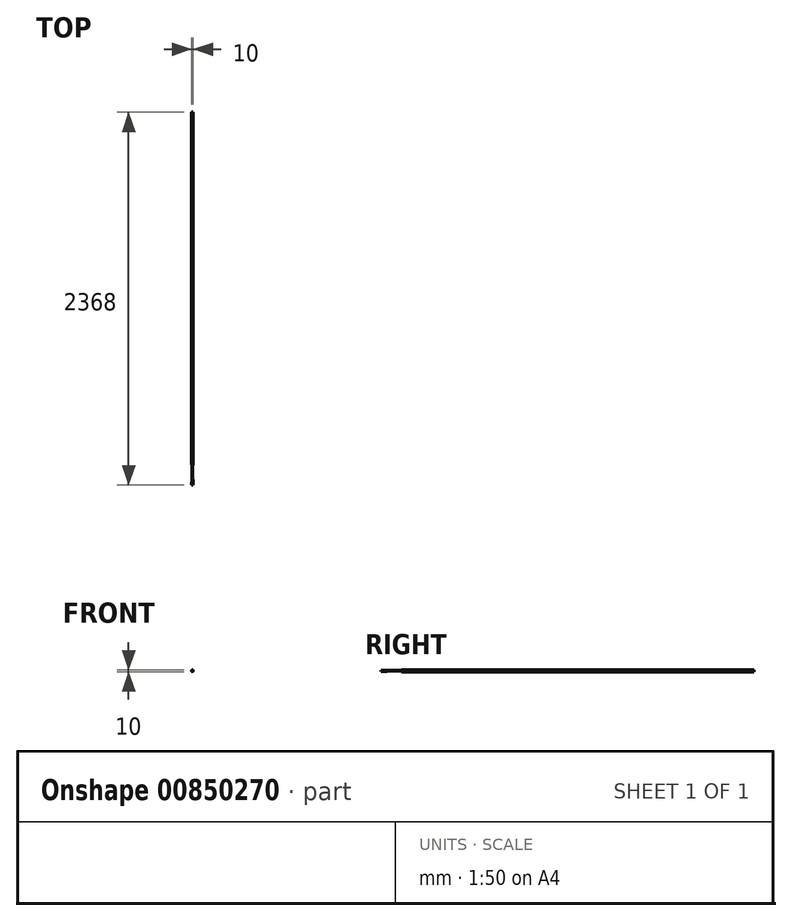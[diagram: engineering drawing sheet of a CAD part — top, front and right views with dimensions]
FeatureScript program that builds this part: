
annotation { "Feature Type Name" : "Feature", "Feature Type Description" : "" }
export const myFeature = defineFeature(function(context is Context, id is Id, definition is map)
    precondition{}
    {
        {
            var Q0;
            Q0=qCreatedBy(makeId("Front.planeOp"),FACE);
            var sketch = newSketch(context, id + "F0", { "sketchPlane" : qUnion([Q0])});
            skLineSegment(sketch, "E0.bottom", {"start": v(5, 3.5) * mm, "end": v(-5, 3.5) * mm});
            skLineSegment(sketch, "E0.top", {"start": v(5, -3.5) * mm, "end": v(-5, -3.5) * mm});
            skLineSegment(sketch, "E0.left", {"start": v(5, 3.5) * mm, "end": v(5, -3.5) * mm});
            skLineSegment(sketch, "E0.right", {"start": v(-5, 3.5) * mm, "end": v(-5, -3.5) * mm});
            skPoint(sketch, "E0.middle", {"position": v(0, 0) * mm});
            skSolve(sketch);
        }
        {
            var Q0;
            Q0 = qSketchRegion(id + "F0", true);
            extrude(context, id + "F1", {"entities" : qUnion([Q0]), "depth" : 20 * mm, "offsetDistance" : 25 * mm});
        }
        {
            var Q0;
            Q0=makeQuery(id+"F1.opExtrude","SWEPT_FACE",FACE,{"disambiguationData":[OSD([sQuery(id+"F0.wireOp",EDGE,"E0.bottom")])]});
            var sketch = newSketch(context, id + "F2", { "sketchPlane" : qUnion([Q0])});
            skLineSegment(sketch, "E1", {"start": v(-7.34, -10) * mm, "end": v(9.17, -10) * mm, "construction": true});
            skLineSegment(sketch, "E2.bottom", {"start": v(2.5, -2) * mm, "end": v(-2.5, -2) * mm});
            skLineSegment(sketch, "E2.top", {"start": v(2.5, -18) * mm, "end": v(-2.5, -18) * mm});
            skLineSegment(sketch, "E2.left", {"start": v(2.5, -2) * mm, "end": v(2.5, -18) * mm});
            skLineSegment(sketch, "E2.right", {"start": v(-2.5, -2) * mm, "end": v(-2.5, -18) * mm});
            skPoint(sketch, "E2.middle", {"position": v(0, -10) * mm});
            skPoint(sketch, "E2.middle.positionSnap0", {"position": v(0.91, -10) * mm});
            skPoint(sketch, "E2.centerSnap0", {"position": v(0.91, -10) * mm});
            skSolve(sketch);
        }
        {
            var Q0;
            Q0 = qSketchRegion(id + "F2", true);
            var Q1;
            Q1=makeQuery(id+"F1.opExtrude","SWEPT_FACE",FACE,{"disambiguationData":[OSD([sQuery(id+"F0.wireOp",EDGE,"E0.top")])]});
            extrude(context, id + "F3", {"entities" : qUnion([Q0]), "operationType" : NewBodyOperationType.REMOVE, "endBound" : BoundingType.UP_TO_SURFACE, "oppositeDirection" : true, "depth" : 10 * mm, "endBoundEntityFace" : qUnion([Q1]), "offsetDistance" : 25 * mm});
        }
        {
            var Q0;
            Q0=makeQuery(id+"F1.opExtrude","SWEPT_FACE",FACE,{"disambiguationData":[OSD([sQuery(id+"F0.wireOp",EDGE,"E0.top")])]});
            var sketch = newSketch(context, id + "F4", { "sketchPlane" : qUnion([Q0])});
            skLineSegment(sketch, "E3.bottom", {"start": v(2.5, 2) * mm, "end": v(-2.5, 2) * mm});
            skLineSegment(sketch, "E3.top", {"start": v(2.5, 5) * mm, "end": v(-2.5, 5) * mm});
            skLineSegment(sketch, "E3.left", {"start": v(2.5, 2) * mm, "end": v(2.5, 5) * mm});
            skLineSegment(sketch, "E3.right", {"start": v(-2.5, 2) * mm, "end": v(-2.5, 5) * mm});
            skLineSegment(sketch, "E4.bottom", {"start": v(-2.5, 18) * mm, "end": v(2.5, 18) * mm});
            skLineSegment(sketch, "E4.top", {"start": v(-2.5, 15) * mm, "end": v(2.5, 15) * mm});
            skLineSegment(sketch, "E4.left", {"start": v(-2.5, 18) * mm, "end": v(-2.5, 15) * mm});
            skLineSegment(sketch, "E4.right", {"start": v(2.5, 18) * mm, "end": v(2.5, 15) * mm});
            skSolve(sketch);
        }
        {
            var Q0;
            Q0 = qSketchRegion(id + "F4", true);
            var Q1;
            Q1=makeQuery(id+"F1.opExtrude","SWEPT_FACE",FACE,{"disambiguationData":[OSD([sQuery(id+"F0.wireOp",EDGE,"E0.bottom")])]});
            extrude(context, id + "F5", {"entities" : qUnion([Q0]), "operationType" : NewBodyOperationType.ADD, "endBound" : BoundingType.UP_TO_SURFACE, "oppositeDirection" : true, "depth" : 25 * mm, "endBoundEntityFace" : qUnion([Q1]), "offsetDistance" : 25 * mm});
        }
        {
            var Q0;
            Q0=makeQuery(id+"F3.boolean.opBoolean","COPY",FACE,{"derivedFrom":makeQuery(id+"F3.opExtrude","SWEPT_FACE",FACE,{"disambiguationData":[OSD([sQuery(id+"F2.wireOp",EDGE,"E2.left")])]})});
            var sketch = newSketch(context, id + "F6", { "sketchPlane" : qUnion([Q0])});
            skLineSegment(sketch, "E5", {"start": v(5, 1.84) * mm, "end": v(2.5, 3.5) * mm});
            skLineSegment(sketch, "E6", {"start": v(2.5, 3.5) * mm, "end": v(5, 3.5) * mm});
            skLineSegment(sketch, "E7", {"start": v(5, 3.5) * mm, "end": v(5, 1.84) * mm});
            skLineSegment(sketch, "E8", {"start": v(0, 0) * mm, "end": v(5.72, 0) * mm, "construction": true});
            skLineSegment(sketch, "E9.MirrorCS", {"start": v(5, -3.5) * mm, "end": v(5, -1.84) * mm});
            skLineSegment(sketch, "E10.MirrorCS", {"start": v(5, -1.84) * mm, "end": v(2.5, -3.5) * mm});
            skLineSegment(sketch, "E11.MirrorCS", {"start": v(2.5, -3.5) * mm, "end": v(5, -3.5) * mm});
            skLineSegment(sketch, "E12", {"start": v(10, 3.4) * mm, "end": v(10, -3.3) * mm, "construction": true});
            skPoint(sketch, "E12.startSnap0", {"position": v(10, 3.5) * mm});
            skLineSegment(sketch, "E13.MirrorCS", {"start": v(15, -3.5) * mm, "end": v(15, -1.84) * mm});
            skLineSegment(sketch, "E14.MirrorCS", {"start": v(15, -1.84) * mm, "end": v(17.5, -3.5) * mm});
            skLineSegment(sketch, "E15.MirrorCS", {"start": v(15, 3.5) * mm, "end": v(15, 1.84) * mm});
            skLineSegment(sketch, "E16.MirrorCS", {"start": v(15, 1.84) * mm, "end": v(17.5, 3.5) * mm});
            skLineSegment(sketch, "E17.MirrorCS", {"start": v(17.5, 3.5) * mm, "end": v(15, 3.5) * mm});
            skSolve(sketch);
        }
        {
            var Q0;
            Q0 = qSketchRegion(id + "F6", true);
            var Q1;
            Q1=makeQuery(id+"F3.boolean.opBoolean","COPY",FACE,{"derivedFrom":makeQuery(id+"F3.opExtrude","SWEPT_FACE",FACE,{"disambiguationData":[OSD([sQuery(id+"F2.wireOp",EDGE,"E2.right")])]})});
            extrude(context, id + "F7", {"entities" : qUnion([Q0]), "operationType" : NewBodyOperationType.REMOVE, "endBound" : BoundingType.UP_TO_SURFACE, "depth" : 25 * mm, "endBoundEntityFace" : qUnion([Q1]), "offsetDistance" : 25 * mm});
        }
        {
            var Q0;
            Q0=makeQuery(id+"F1.opExtrude","CAP_FACE",FACE,{"disambiguationData":[OSD([sQuery(id+"F0.wireOp",EDGE,"E0.bottom"),sQuery(id+"F0.wireOp",EDGE,"E0.top"),sQuery(id+"F0.wireOp",EDGE,"E0.left"),sQuery(id+"F0.wireOp",EDGE,"E0.right")])],"isStart":true});
            var sketch = newSketch(context, id + "F8", { "sketchPlane" : qUnion([Q0])});
            skCircle(sketch, "E18", {"center": v(0, 0) * mm, "radius": 3.5 * mm});
            skSolve(sketch);
        }
        {
            var Q0;
            {var subQ0=sQuery(id+"F8.wireOp",EDGE,"E18");var subQ1=makeQuery(id+"F8.imprint","INTERSECT",VERTEX,{"derivedFrom":[makeQuery(id+"F1.opExtrude","CAP_EDGE",EDGE,{"disambiguationData":[OSD([sQuery(id+"F0.wireOp",EDGE,"E0.bottom")])],"isStart":true}),subQ0]});Q0=makeQuery(id+"F8.imprint","IMPRINT",FACE,{"disambiguationData":[TD([[makeQuery(id+"F8.imprint","IMPRINT",EDGE,{"disambiguationData":[TD([[subQ1,-1.0]])],"derivedFrom":subQ0}),1.0]])]});}
            extrude(context, id + "F9", {"entities" : qUnion([Q0]), "operationType" : NewBodyOperationType.ADD, "depth" : 16 * mm, "offsetDistance" : 25 * mm});
        }
        {
            var Q0;
            Q0=makeQuery(id+"F9.opExtrude","CAP_FACE",FACE,{"disambiguationData":[OSD([sQuery(id+"F8.wireOp",EDGE,"E18")])],"isStart":false});
            var sketch = newSketch(context, id + "F10", { "sketchPlane" : qUnion([Q0])});
            skCircle(sketch, "E19", {"center": v(0, 0) * mm, "radius": 1.5 * mm});
            skSolve(sketch);
        }
        {
            var Q0;
            Q0 = qSketchRegion(id + "F10", true);
            extrude(context, id + "F11", {"entities" : qUnion([Q0]), "operationType" : NewBodyOperationType.ADD, "depth" : 94 * mm, "offsetDistance" : 25 * mm});
        }
        {
            var Q0;
            Q0=makeQuery(id+"F11.opExtrude","CAP_FACE",FACE,{"disambiguationData":[OSD([sQuery(id+"F10.wireOp",EDGE,"E19")])],"isStart":false});
            var sketch = newSketch(context, id + "F12", { "sketchPlane" : qUnion([Q0])});
            skCircle(sketch, "E20", {"center": v(0, 0) * mm, "radius": 5 * mm});
            skSolve(sketch);
        }
        {
            var Q0;
            Q0 = qSketchRegion(id + "F12", true);
            extrude(context, id + "F13", {"entities" : qUnion([Q0]), "operationType" : NewBodyOperationType.ADD, "depth" : 2238 * mm, "offsetDistance" : 25 * mm});
        }
    });
